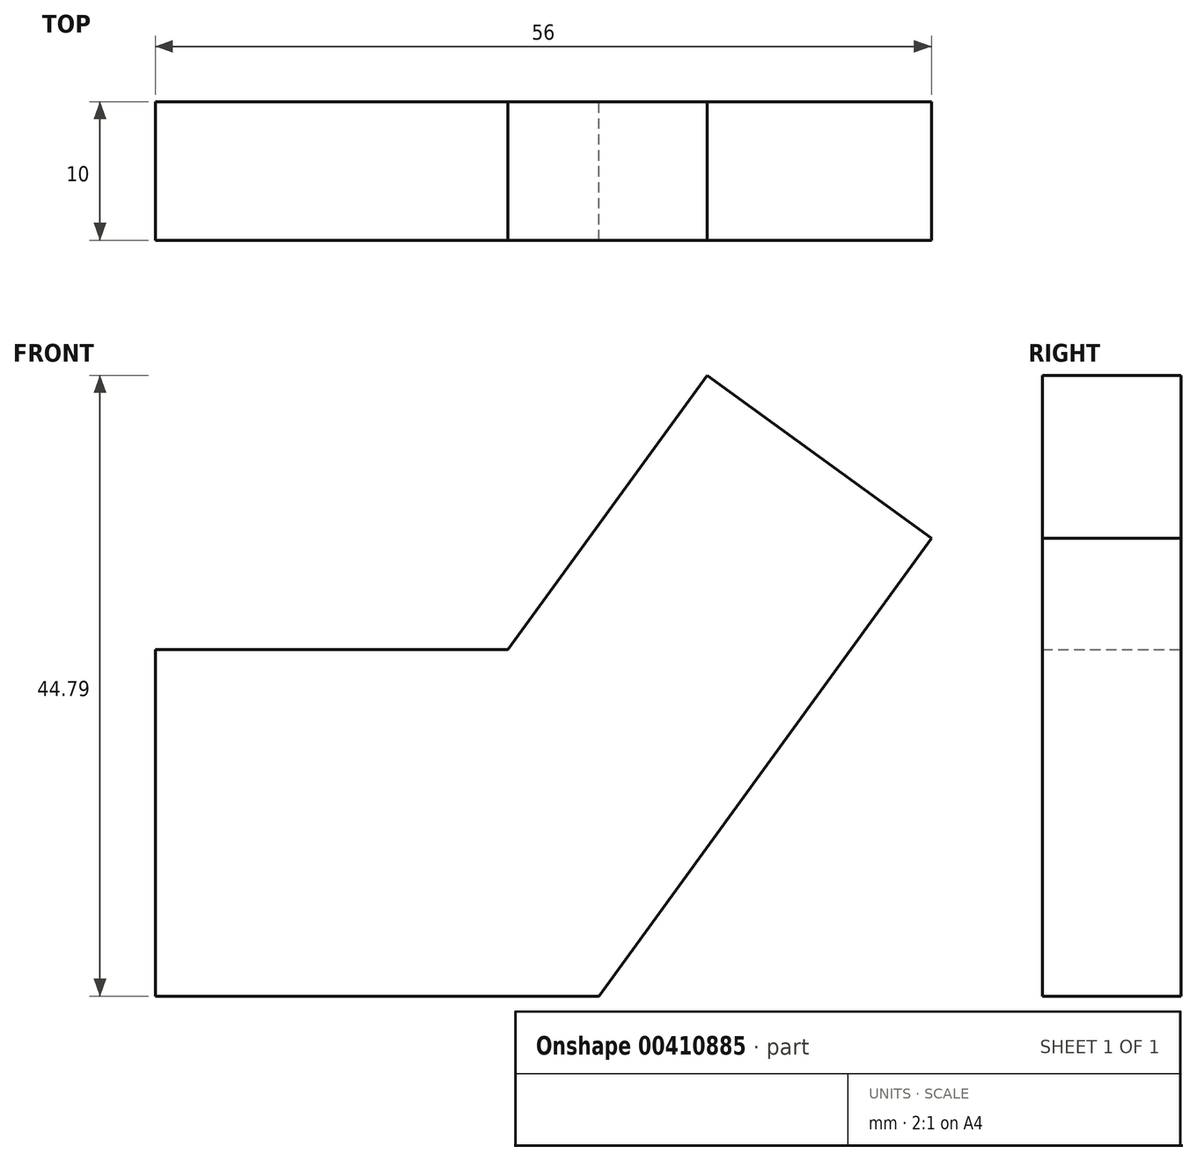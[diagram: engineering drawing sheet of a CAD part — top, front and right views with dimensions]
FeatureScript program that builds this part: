
annotation { "Feature Type Name" : "Feature", "Feature Type Description" : "" }
export const myFeature = defineFeature(function(context is Context, id is Id, definition is map)
    precondition{}
    {
        {
            var Q0;
            Q0=qCreatedBy(makeId("Front.planeOp"),FACE);
            var sketch = newSketch(context, id + "F0", { "sketchPlane" : qUnion([Q0])});
            skLineSegment(sketch, "E0", {"start": v(0, 0) * mm, "end": v(32, 0) * mm});
            skLineSegment(sketch, "E1", {"start": v(32, 0) * mm, "end": v(56, 33.03) * mm});
            skLineSegment(sketch, "E2", {"start": v(56, 33.03) * mm, "end": v(39.82, 44.79) * mm});
            skLineSegment(sketch, "E3", {"start": v(39.82, 44.79) * mm, "end": v(25.44, 25) * mm});
            skLineSegment(sketch, "E4", {"start": v(25.44, 25) * mm, "end": v(0, 25) * mm});
            skLineSegment(sketch, "E5", {"start": v(0, 25) * mm, "end": v(0, 0) * mm});
            skSolve(sketch);
        }
        {
            var Q0;
            Q0 = qSketchRegion(id + "F0", true);
            extrude(context, id + "F1", {"entities" : qUnion([Q0]), "endBound" : BoundingType.SYMMETRIC, "depth" : 10 * mm});
        }
    });
